# Revit family: PRD_FrankeWS_SpprtRls_CornerBar_CNTX52W
name_source: partatom
category: Specialty Equipment
revit_build: Autodesk Revit 2018 (Build: 20190510_1515(x64)
units: mm (PartAtom-declared; Revit-internal decimal feet)

## family parameters
Cut with Voids When Loaded = No
Host = Face
OmniClass Number = 23.40.20.21
OmniClass Title = Toilet and Bath Specialties
Part Type = Normal
Room Calculation Point = No
Round Connector Dimension = Use Diameter
Shared = No

## types (1)
- CNTX52W
    AssetType = Fixed
    BIMObjectName = PRD_AR_SupportRails_CornerBar_CNTX52W
    Back = No
    BendingAngle = 90.00 degree
    Category = Pr_40_20_76_84, Support rails
    Color = no color
    Default Elevation = 750 mm  [stored 2.46063 ft]
    Description = Horizontal corner bar for wall mounting, stainless steel, surface satin finished, rough polishing for better surface feel, 32 mm pipe diameter, material thickness 1.2 mm, wall distance 82 mm, with three stainless steel covers for hidden mounting, includes stainless steel screws and dowels.
    DurationUnit = year
    Features = stainless steel, surface satin finished
    Finish = satin finished
    GrabRailMaterial = PRD_AR_StainlessSteel_SatinFinished
    GrossWeight = 1.73 kg
    HiddenFixing = Yes
    Hinged = No
    IfcExportAs = IfcFurnitureType
    IfcExportType = USERDEFINED
    IntegralAccessories = incl. stainless steel screws and dowels
    IsBuiltIn = TRUE
    MainColor = stainless steel
    Manufacturer = KWC Group AG
    ManufacturerName = KWC Group AG
    ManufacturerURL = www.kwc.com
    Material = stainless steel
    MaterialCode = 1.4301
    MaterialThickness = 1.20 mm
    Model = CNTX52W
    ModelNumber = 2030036235
    ModelReference = CNTX52W
    NBSDescription = Support rails
    NBSReference = 45-35-72/360
    Name = Corner Bar CNTX52W
    NetWeight = 1.61 kg
    NominalDepth = 726 mm  [stored 2.38189 ft]
    NominalHeight = 78 mm  [stored 0.255906 ft]
    NominalWidth = 726 mm  [stored 2.38189 ft]
    PipeDiameter = 32  [stored 0.104987 ft]
    ProductInformation = https://pim.kwc.com
    Size = 726 x 78 x 726 mm
    TypeOfFixing = Screw
    TypeOfGrabRail = Corner bar
    TypeOfMounting = Wall mounting
    URL = www.kwc.com
    Uniclass2015Code = Pr_40_20_76_84
    Uniclass2015Title = Support rails
    Uniclass2015Version = Products v1.10
    Version = 1
    WarrantyDurationUnit = year

note: [stored X ft] marks values corroborated as IEEE doubles in the binary element streams (Revit-internal decimal feet)

## geometry (parser evidence)
native form markers: Sweep x5
no freeform markers — native parametric forms only
